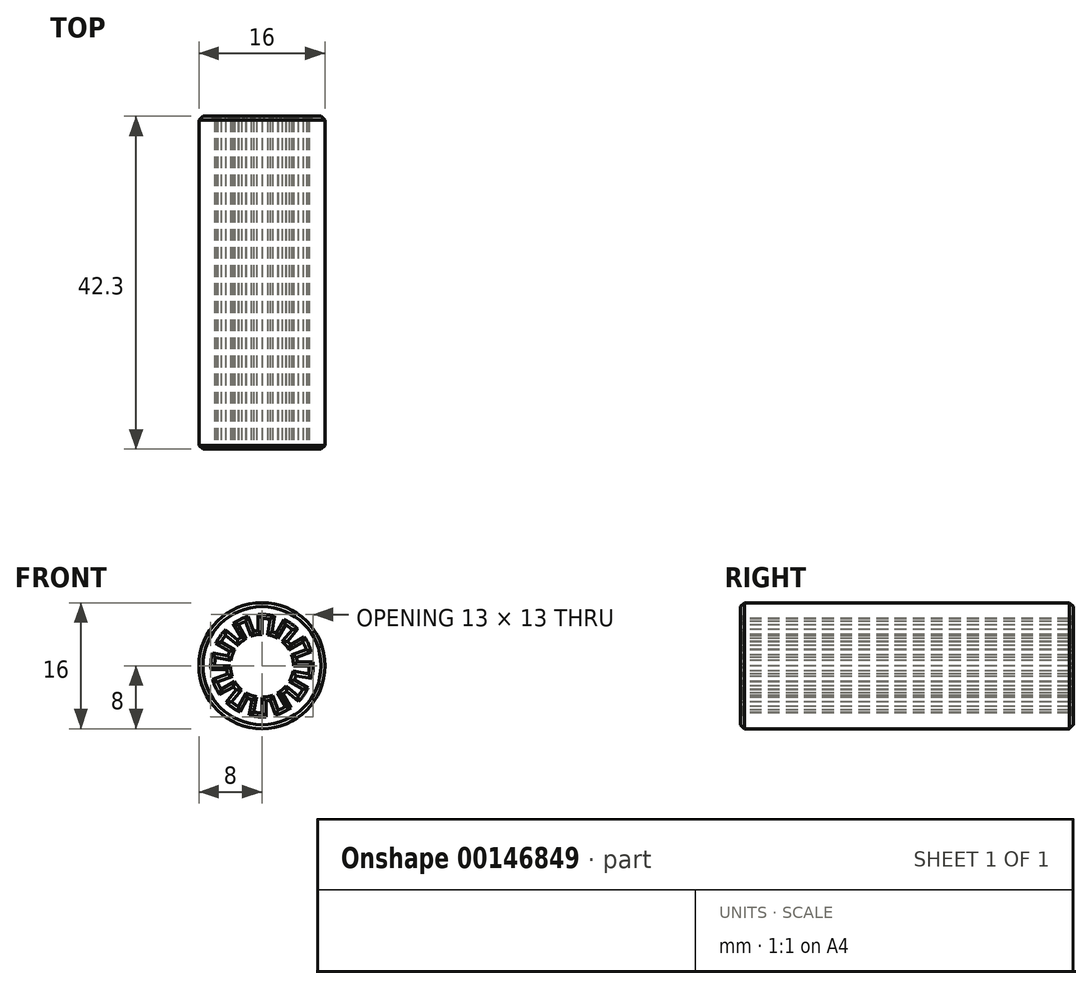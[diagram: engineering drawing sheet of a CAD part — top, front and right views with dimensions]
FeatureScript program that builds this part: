
annotation { "Feature Type Name" : "Feature", "Feature Type Description" : "" }
export const myFeature = defineFeature(function(context is Context, id is Id, definition is map)
    precondition{}
    {
        {
            var Q0;
            Q0=qCreatedBy(makeId("Front.planeOp"),FACE);
            var sketch = newSketch(context, id + "F0", { "sketchPlane" : qUnion([Q0])});
            skCircle(sketch, "E0", {"center": v(0, 0) * mm, "radius": 8 * mm});
            skCircle(sketch, "E1", {"center": v(0, 0) * mm, "radius": 6 * mm});
            skCircle(sketch, "E2", {"center": v(0, 0) * mm, "radius": 4 * mm});
            skLineSegment(sketch, "E3", {"start": v(4, 0) * mm, "end": v(8, 0) * mm});
            skLineSegment(sketch, "E4", {"start": v(0, 0) * mm, "end": v(7.52, 2.74) * mm, "construction": true});
            skLineSegment(sketch, "E5", {"start": v(7.52, 2.74) * mm, "end": v(0, 0) * mm, "construction": true});
            skLineSegment(sketch, "E6", {"start": v(0, 0) * mm, "end": v(6.93, 4) * mm, "construction": true});
            skLineSegment(sketch, "E7", {"start": v(3.76, 1.37) * mm, "end": v(5.64, 2.05) * mm});
            skLineSegment(sketch, "E8", {"start": v(5.2, 3) * mm, "end": v(6.93, 4) * mm});
            skSolve(sketch);
        }
        {
            var Q0;
            {var subQ0=sQuery(id+"F0.wireOp",EDGE,"E7");Q0=makeQuery(id+"F0.imprint","IMPRINT",FACE,{"disambiguationData":[TD([[makeQuery(id+"F0.imprint","IMPRINT",EDGE,{"derivedFrom":subQ0}),-1.0]])]});}
            var Q1;
            {var subQ6=sQuery(id+"F0.wireOp",EDGE,"E8");Q1=makeQuery(id+"F0.imprint","IMPRINT",FACE,{"disambiguationData":[TD([[makeQuery(id+"F0.imprint","IMPRINT",EDGE,{"derivedFrom":subQ6}),-1.0]])]});}
            extrude(context, id + "F1", {"entities" : qUnion([Q0, Q1]), "oppositeDirection" : true, "depth" : 42.3 * mm});
        }
        {
            var Q0;
            Q0=qCreatedBy(makeId("Top.planeOp"),FACE);
            var sketch = newSketch(context, id + "F2", { "sketchPlane" : qUnion([Q0])});
            skLineSegment(sketch, "E9", {"start": v(0, 0) * mm, "end": v(0, 52.43) * mm, "construction": true});
            skSolve(sketch);
        }
        {
            var Q0;
            Q0=makeQuery(id+"F1.opExtrude","SWEPT_BODY",BODY,{"disambiguationData":[OSD([sQuery(id+"F0.wireOp",EDGE,"E0"),sQuery(id+"F0.wireOp",EDGE,"E1"),sQuery(id+"F0.wireOp",EDGE,"E2"),sQuery(id+"F0.wireOp",EDGE,"E3"),sQuery(id+"F0.wireOp",EDGE,"E7"),sQuery(id+"F0.wireOp",EDGE,"E8")])]});
            var Q1;
            Q1=sQuery(id+"F2.wireOp",EDGE,"E9");
            circularPattern(context, id + "F3", {"operationType" : NewBodyOperationType.ADD, "entities" : qUnion([Q0]), "axis" : qUnion([Q1]), "angle" : 30 * degree, "instanceCount" : 12});
        }
        {
            var Q0;
            {var subQ0=makeQuery(id+"F1.opExtrude","CAP_FACE",FACE,{"disambiguationData":[OSD([sQuery(id+"F0.wireOp",EDGE,"E0"),sQuery(id+"F0.wireOp",EDGE,"E1"),sQuery(id+"F0.wireOp",EDGE,"E2"),sQuery(id+"F0.wireOp",EDGE,"E3"),sQuery(id+"F0.wireOp",EDGE,"E7"),sQuery(id+"F0.wireOp",EDGE,"E8")])],"isStart":false});Q0=makeQuery(id+"F3.boolean.opBoolean","MERGE",FACE,{"derivedFrom":[subQ0,makeQuery(id+"F3.opPattern","COPY",FACE,{"derivedFrom":subQ0,"instanceName":"1"}),makeQuery(id+"F3.opPattern","COPY",FACE,{"derivedFrom":subQ0,"instanceName":"2"}),makeQuery(id+"F3.opPattern","COPY",FACE,{"derivedFrom":subQ0,"instanceName":"3"}),makeQuery(id+"F3.opPattern","COPY",FACE,{"derivedFrom":subQ0,"instanceName":"4"}),makeQuery(id+"F3.opPattern","COPY",FACE,{"derivedFrom":subQ0,"instanceName":"5"}),makeQuery(id+"F3.opPattern","COPY",FACE,{"derivedFrom":subQ0,"instanceName":"6"}),makeQuery(id+"F3.opPattern","COPY",FACE,{"derivedFrom":subQ0,"instanceName":"7"}),makeQuery(id+"F3.opPattern","COPY",FACE,{"derivedFrom":subQ0,"instanceName":"8"}),makeQuery(id+"F3.opPattern","COPY",FACE,{"derivedFrom":subQ0,"instanceName":"9"}),makeQuery(id+"F3.opPattern","COPY",FACE,{"derivedFrom":subQ0,"instanceName":"10"}),makeQuery(id+"F3.opPattern","COPY",FACE,{"derivedFrom":subQ0,"instanceName":"11"})]});}
            var Q1;
            {var subQ0=makeQuery(id+"F1.opExtrude","CAP_FACE",FACE,{"disambiguationData":[OSD([sQuery(id+"F0.wireOp",EDGE,"E0"),sQuery(id+"F0.wireOp",EDGE,"E1"),sQuery(id+"F0.wireOp",EDGE,"E2"),sQuery(id+"F0.wireOp",EDGE,"E3"),sQuery(id+"F0.wireOp",EDGE,"E7"),sQuery(id+"F0.wireOp",EDGE,"E8")])],"isStart":true});Q1=makeQuery(id+"F3.boolean.opBoolean","MERGE",FACE,{"derivedFrom":[subQ0,makeQuery(id+"F3.opPattern","COPY",FACE,{"derivedFrom":subQ0,"instanceName":"1"}),makeQuery(id+"F3.opPattern","COPY",FACE,{"derivedFrom":subQ0,"instanceName":"2"}),makeQuery(id+"F3.opPattern","COPY",FACE,{"derivedFrom":subQ0,"instanceName":"3"}),makeQuery(id+"F3.opPattern","COPY",FACE,{"derivedFrom":subQ0,"instanceName":"4"}),makeQuery(id+"F3.opPattern","COPY",FACE,{"derivedFrom":subQ0,"instanceName":"5"}),makeQuery(id+"F3.opPattern","COPY",FACE,{"derivedFrom":subQ0,"instanceName":"6"}),makeQuery(id+"F3.opPattern","COPY",FACE,{"derivedFrom":subQ0,"instanceName":"7"}),makeQuery(id+"F3.opPattern","COPY",FACE,{"derivedFrom":subQ0,"instanceName":"8"}),makeQuery(id+"F3.opPattern","COPY",FACE,{"derivedFrom":subQ0,"instanceName":"9"}),makeQuery(id+"F3.opPattern","COPY",FACE,{"derivedFrom":subQ0,"instanceName":"10"}),makeQuery(id+"F3.opPattern","COPY",FACE,{"derivedFrom":subQ0,"instanceName":"11"})]});}
            chamfer(context, id + "F4", {"entities" : qUnion([Q0, Q1]), "width" : 0.5 * mm, "tangentPropagation" : true});
        }
    });
